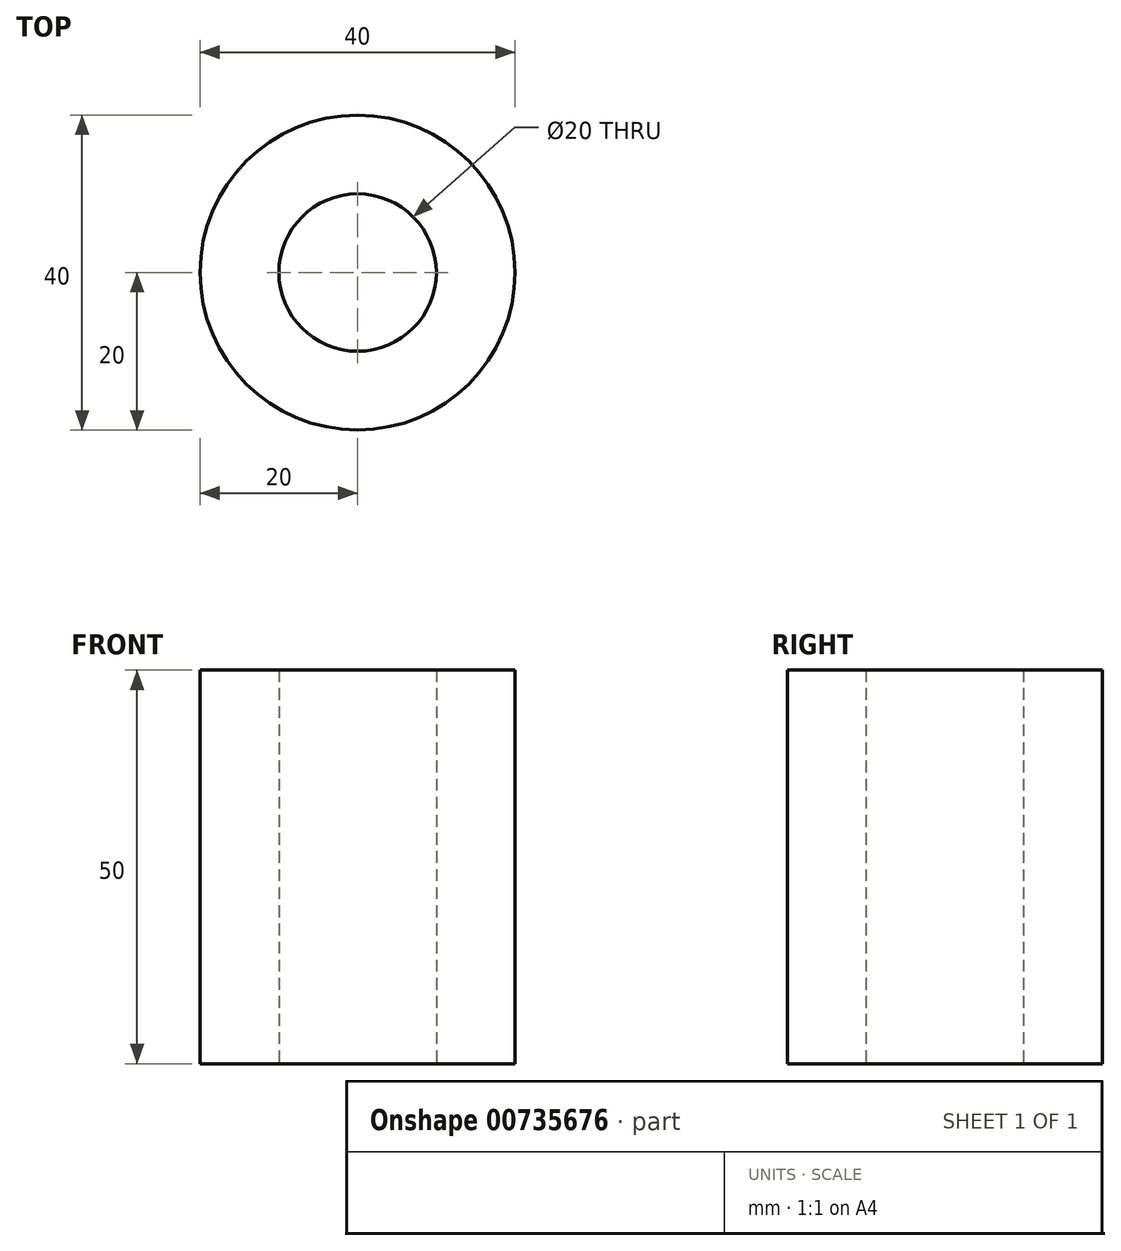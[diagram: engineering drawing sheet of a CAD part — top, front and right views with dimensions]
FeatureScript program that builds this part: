
annotation { "Feature Type Name" : "Feature", "Feature Type Description" : "" }
export const myFeature = defineFeature(function(context is Context, id is Id, definition is map)
    precondition{}
    {
        {
            var Q0;
            Q0=qCreatedBy(makeId("Top.planeOp"),FACE);
            var sketch = newSketch(context, id + "F0", { "sketchPlane" : qUnion([Q0])});
            skCircle(sketch, "E0", {"center": v(0, 0) * mm, "radius": 10 * mm});
            skCircle(sketch, "E1", {"center": v(0, 0) * mm, "radius": 20 * mm});
            skSolve(sketch);
        }
        {
            var Q0;
            Q0=makeQuery(id+"F0.imprint","IMPRINT",FACE,{"disambiguationData":[TD([[makeQuery(id+"F0.imprint","IMPRINT",EDGE,{"derivedFrom":sQuery(id+"F0.wireOp",EDGE,"E0")}),-1.0]])]});
            extrude(context, id + "F1", {"entities" : qUnion([Q0]), "endBound" : BoundingType.SYMMETRIC, "depth" : 50 * mm, "offsetDistance" : 25 * mm});
        }
    });
